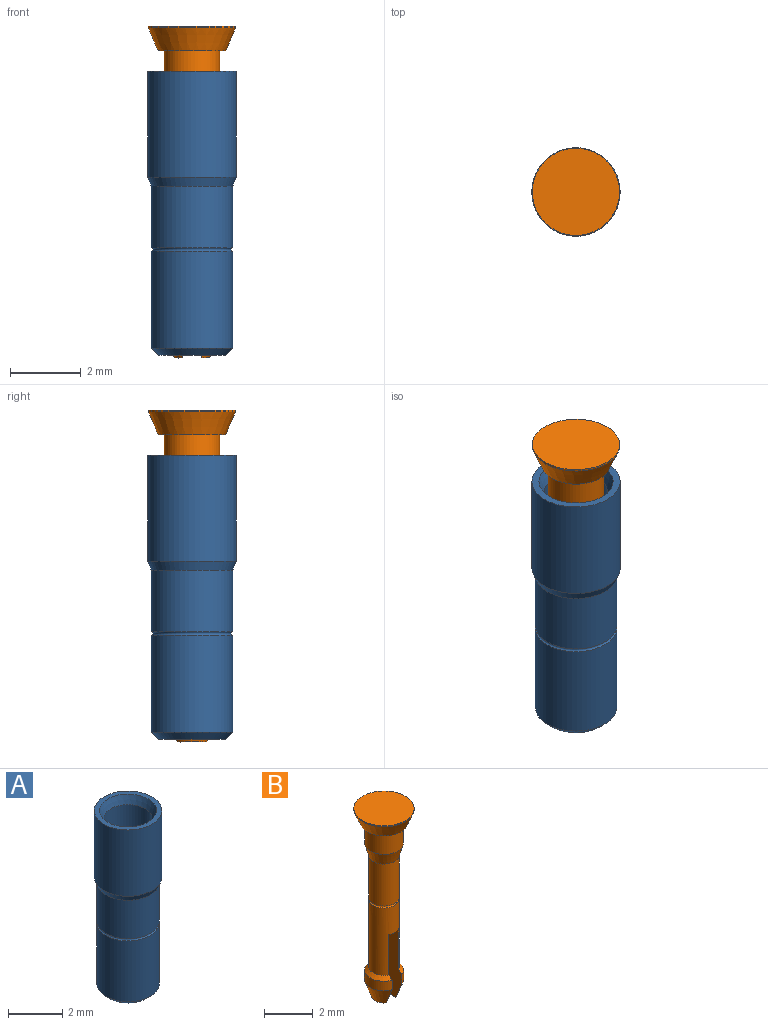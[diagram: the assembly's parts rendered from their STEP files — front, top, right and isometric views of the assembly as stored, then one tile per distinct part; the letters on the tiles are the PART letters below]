
ASSEMBLY  parts=2 mates=1
PART A: 12 faces, bbox 2.6x2.6x8 mm
  f0: torus R=1.15mm, axis (0,0,1), area 1.1mm2, adj f1,f11
  f1: cylinder r=1.15mm len=2.75mm, axis (0,0,1), area 19.9mm2, adj f0,f2
  f2: cone r=0.95mm half-angle=45deg, axis (0,0,1), area 1.9mm2, adj f1,f3
  f3: plane 1.9x1.9mm, normal (0,0,-1), area 1.4mm2, adj f2,f4
  f4: cylinder r=0.68mm len=1.35mm, axis (0,0,1), area 4.4mm2, adj f3,f5
  f5: cone r=0.9mm half-angle=60deg, axis (0,0,1), area 1.3mm2, adj f4,f6
  f6: cylinder r=0.9mm len=6.51mm, axis (0,0,1), area 36.8mm2, adj f5,f7
  f7: cone r=1.05mm half-angle=22deg, axis (0,0,1), area 2.5mm2, adj f6,f8
  f8: plane 2.5x2.5mm, normal (0,0,1), area 1.4mm2, adj f7,f9
  f9: cylinder r=1.25mm len=3mm, axis (0,0,1), area 23.6mm2, adj f8,f10
  f10: cone r=1.25mm half-angle=22deg, axis (0,0,1), area 2mm2, adj f9,f11
  f11: cylinder r=1.15mm len=2.3mm, axis (0,0,1), area 12.6mm2, adj f0,f10
PART B: 20 faces, bbox 2.5x2.5x9.4 mm
  f0: cylinder r=0.8mm len=1.5mm, axis (0,0,1), area 0.9mm2, adj f1,f3,f19
  f1: cone r=0.8mm half-angle=20deg, axis (0,0,1), area 1.3mm2, adj f0,f2,f19
  f2: plane 0.84x0.23mm, normal (0,0,-1), area 0.1mm2, adj f1,f19
  f3: cone r=0.62mm half-angle=45deg, axis (0,0,-1), area 0.4mm2, adj f0,f15,f19
  f4: cylinder r=0.8mm len=1.5mm, axis (0,0,1), area 0.9mm2, adj f5,f16,f17
  f5: cone r=0.8mm half-angle=20deg, axis (0,0,1), area 1.3mm2, adj f4,f6,f17
  f6: plane 0.84x0.23mm, normal (0,0,-1), area 0.1mm2, adj f5,f17
  f7: plane 2.47x2.47mm, normal (0,0,1), area 4.8mm2, adj f8
  f8: cylinder r=1.23mm len=2.47mm, axis (0,0,1), area 0.4mm2, adj f7,f9
  f9: cone r=1.23mm half-angle=23deg, axis (0,0,1), area 4.9mm2, adj f8,f10
  f10: plane 1.92x1.92mm, normal (0,0,-1), area 1mm2, adj f9,f11
  f11: cylinder r=0.79mm len=1.57mm, axis (0,0,1), area 5.2mm2, adj f10,f12
  f12: cone r=0.79mm half-angle=15deg, axis (0,0,1), area 2.7mm2, adj f11,f13
  f13: cylinder r=0.62mm len=2.1mm, axis (0,0,1), area 8.3mm2, adj f12,f14
  f14: torus R=0.62mm, axis (0,0,1), area 0.6mm2, adj f13,f15
  f15: cylinder r=0.62mm len=3.38mm, axis (0,0,1), area 10.9mm2, adj f3,f14,f16,f17,f18,f19
  f16: cone r=0.62mm half-angle=45deg, axis (0,0,-1), area 0.4mm2, adj f4,f15,f17
  f17: plane 3.54x1.54mm, normal (-1,0,0), area 4.2mm2, adj f4,f5,f6,f15,f16,f18
  f18: plane 1.25x0.55mm, normal (0,0,-1), area 0.7mm2, adj f15,f17,f19
  f19: plane 3.54x1.54mm, normal (1,0,0), area 4.2mm2, adj f0,f1,f2,f3,f15,f18
PLACE A rot(axis=(-0.54,-0.64,0.55),0deg) t=(-3.36,-0.1,-1.93)mm
PLACE B rot(axis=(-0.54,-0.64,0.55),0deg) t=(-3.36,-0.1,-6.8)mm
MATE slider B.f0 <-> A.f0  axis (0,0,1) through (-3.36,-0.1,3.99)mm
